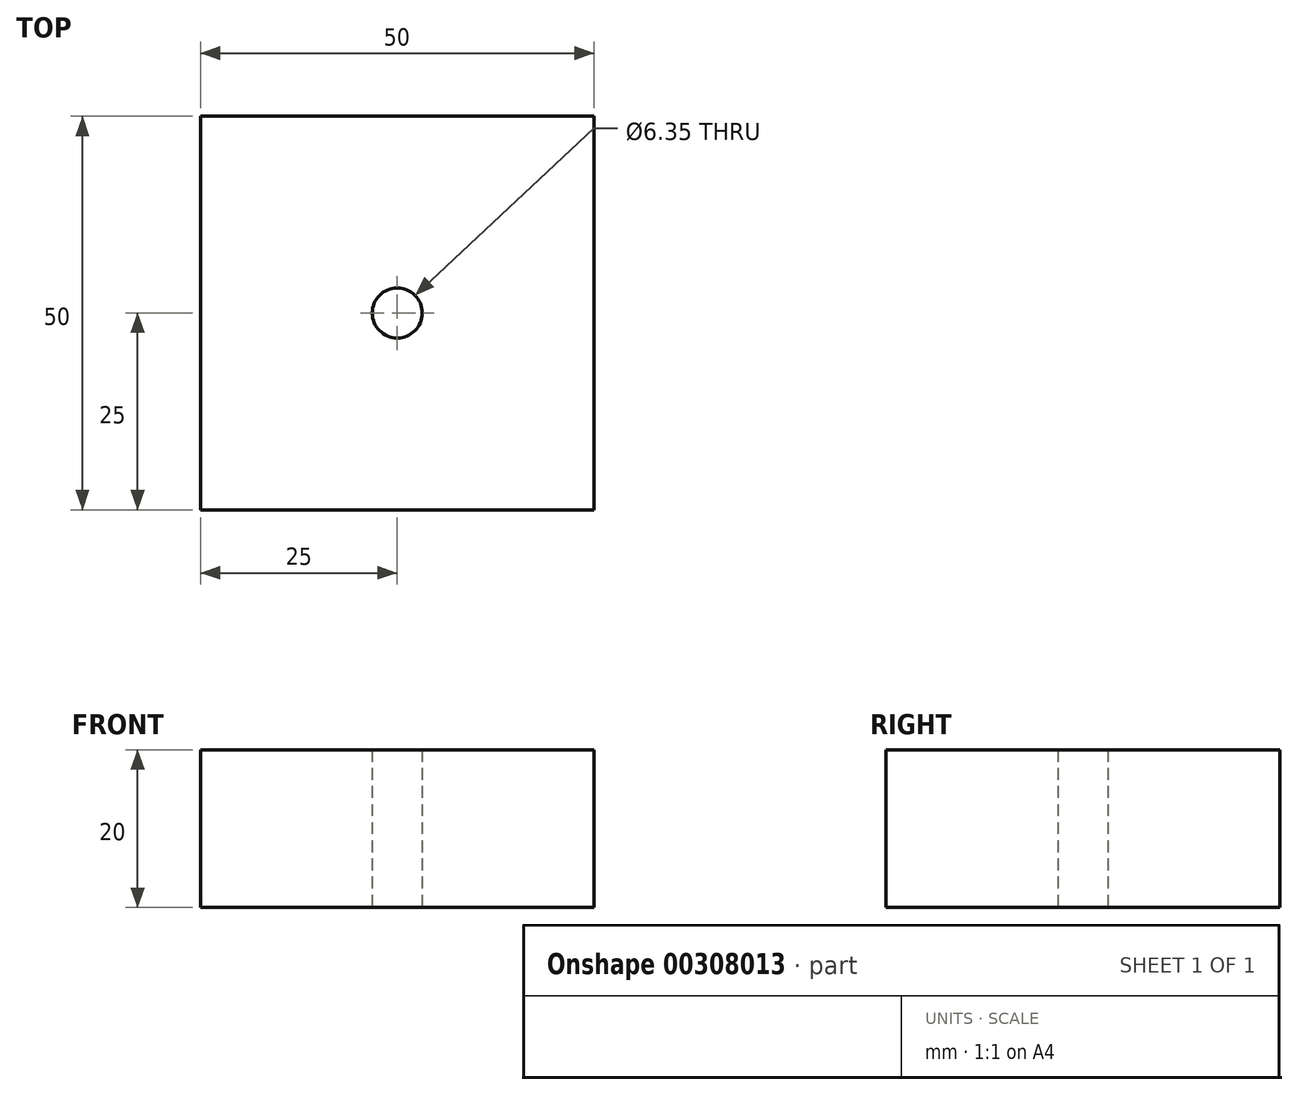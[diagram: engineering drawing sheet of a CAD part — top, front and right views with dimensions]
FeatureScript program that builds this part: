
annotation { "Feature Type Name" : "Feature", "Feature Type Description" : "" }
export const myFeature = defineFeature(function(context is Context, id is Id, definition is map)
    precondition{}
    {
        {
            var Q0;
            Q0=qCreatedBy(makeId("Top.planeOp"),FACE);
            var sketch = newSketch(context, id + "F0", { "sketchPlane" : qUnion([Q0])});
            skLineSegment(sketch, "E0.bottom", {"start": v(25, 25) * mm, "end": v(-25, 25) * mm});
            skLineSegment(sketch, "E0.top", {"start": v(25, -25) * mm, "end": v(-25, -25) * mm});
            skLineSegment(sketch, "E0.left", {"start": v(25, 25) * mm, "end": v(25, -25) * mm});
            skLineSegment(sketch, "E0.right", {"start": v(-25, 25) * mm, "end": v(-25, -25) * mm});
            skPoint(sketch, "E0.middle", {"position": v(0, 0) * mm});
            skCircle(sketch, "E1", {"center": v(0, 0) * mm, "radius": 3.18 * mm});
            skSolve(sketch);
        }
        {
            var Q0;
            Q0=makeQuery(id+"F0.imprint","IMPRINT",FACE,{"disambiguationData":[TD([[makeQuery(id+"F0.imprint","IMPRINT",EDGE,{"derivedFrom":sQuery(id+"F0.wireOp",EDGE,"E0.bottom")}),1.0]])]});
            extrude(context, id + "F1", {"entities" : qUnion([Q0]), "depth" : 20 * mm});
        }
    });
